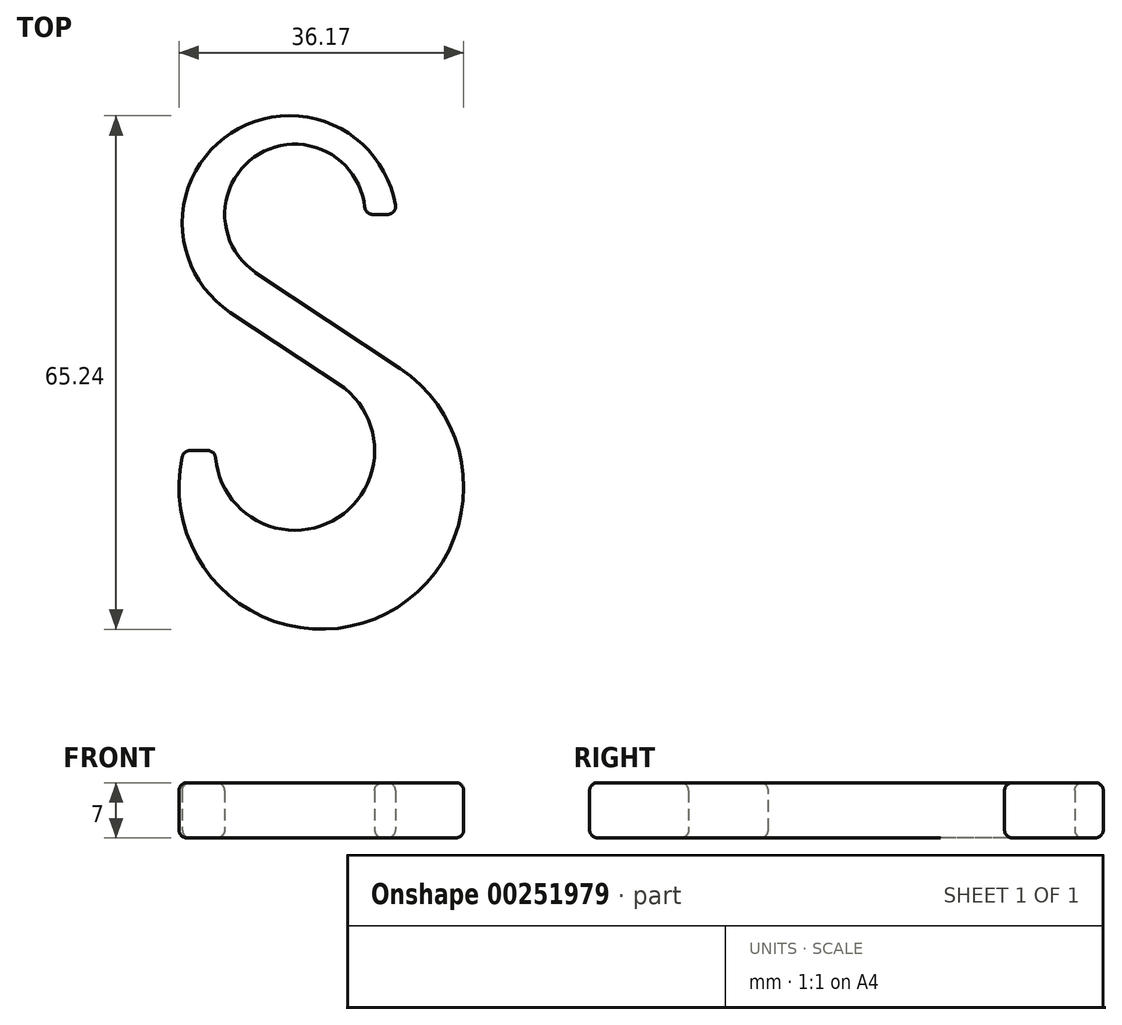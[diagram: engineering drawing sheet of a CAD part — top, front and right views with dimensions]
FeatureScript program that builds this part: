
annotation { "Feature Type Name" : "Feature", "Feature Type Description" : "" }
export const myFeature = defineFeature(function(context is Context, id is Id, definition is map)
    precondition{}
    {
        {
            var Q0;
            Q0=qCreatedBy(makeId("Top.planeOp"),FACE);
            var sketch = newSketch(context, id + "F0", { "sketchPlane" : qUnion([Q0])});
            skArc(sketch, "E0", {"start": v(8.92, 0) * mm, "mid": v(-4.16, 7.89) * mm, "end": v(-5.04, -7.35) * mm});
            skArc(sketch, "E1", {"start": v(-10.13, -30) * mm, "mid": v(4.39, -39.13) * mm, "end": v(6.33, -22.1) * mm});
            skArc(sketch, "E2.0", {"start": v(12.92, 0) * mm, "mid": v(-7.6, 10.65) * mm, "end": v(-8.2, -12.45) * mm});
            skArc(sketch, "E3.0", {"start": v(-14.13, -30) * mm, "mid": v(9.78, -51.52) * mm, "end": v(13.35, -19.55) * mm});
            skLineSegment(sketch, "E4", {"start": v(-5.04, -7.35) * mm, "end": v(13.35, -19.55) * mm});
            skLineSegment(sketch, "E5", {"start": v(-8.2, -12.45) * mm, "end": v(6.33, -22.1) * mm});
            skLineSegment(sketch, "E6", {"start": v(-14.13, -30) * mm, "end": v(-10.13, -30) * mm});
            skLineSegment(sketch, "E7", {"start": v(12.92, 0) * mm, "end": v(8.92, 0) * mm});
            skSolve(sketch);
        }
        {
            var Q0;
            Q0=makeQuery(id+"F0.imprint","IMPRINT",FACE,{"disambiguationData":[TD([[makeQuery(id+"F0.imprint","IMPRINT",EDGE,{"derivedFrom":sQuery(id+"F0.wireOp",EDGE,"E0")}),-1.0]])]});
            extrude(context, id + "F1", {"entities" : qUnion([Q0]), "depth" : 7 * mm});
        }
        {
            var Q0;
            Q0=makeQuery(id+"F1.opExtrude","SWEPT_FACE",FACE,{"disambiguationData":[OSD([sQuery(id+"F0.wireOp",EDGE,"E0")])]});
            var Q1;
            Q1=makeQuery(id+"F1.opExtrude","CAP_FACE",FACE,{"disambiguationData":[OSD([sQuery(id+"F0.wireOp",EDGE,"E0"),sQuery(id+"F0.wireOp",EDGE,"E1"),sQuery(id+"F0.wireOp",EDGE,"E2.0"),sQuery(id+"F0.wireOp",EDGE,"E3.0"),sQuery(id+"F0.wireOp",EDGE,"E4"),sQuery(id+"F0.wireOp",EDGE,"E5"),sQuery(id+"F0.wireOp",EDGE,"E6"),sQuery(id+"F0.wireOp",EDGE,"E7")])],"isStart":true});
            var Q2;
            Q2=makeQuery(id+"F1.opExtrude","CAP_FACE",FACE,{"disambiguationData":[OSD([sQuery(id+"F0.wireOp",EDGE,"E0"),sQuery(id+"F0.wireOp",EDGE,"E1"),sQuery(id+"F0.wireOp",EDGE,"E2.0"),sQuery(id+"F0.wireOp",EDGE,"E3.0"),sQuery(id+"F0.wireOp",EDGE,"E4"),sQuery(id+"F0.wireOp",EDGE,"E5"),sQuery(id+"F0.wireOp",EDGE,"E6"),sQuery(id+"F0.wireOp",EDGE,"E7")])],"isStart":false});
            var Q3;
            Q3=makeQuery(id+"F1.opExtrude","SWEPT_FACE",FACE,{"disambiguationData":[OSD([sQuery(id+"F0.wireOp",EDGE,"E1")])]});
            var Q4;
            Q4=makeQuery(id+"F1.opExtrude","SWEPT_FACE",FACE,{"disambiguationData":[OSD([sQuery(id+"F0.wireOp",EDGE,"E2.0")])]});
            var Q5;
            Q5=makeQuery(id+"F1.opExtrude","SWEPT_FACE",FACE,{"disambiguationData":[OSD([sQuery(id+"F0.wireOp",EDGE,"E3.0")])]});
            var Q6;
            Q6=makeQuery(id+"F1.opExtrude","SWEPT_FACE",FACE,{"disambiguationData":[OSD([sQuery(id+"F0.wireOp",EDGE,"E4")])]});
            var Q7;
            Q7=makeQuery(id+"F1.opExtrude","SWEPT_FACE",FACE,{"disambiguationData":[OSD([sQuery(id+"F0.wireOp",EDGE,"E5")])]});
            var Q8;
            Q8=makeQuery(id+"F1.opExtrude","SWEPT_FACE",FACE,{"disambiguationData":[OSD([sQuery(id+"F0.wireOp",EDGE,"E6")])]});
            var Q9;
            Q9=makeQuery(id+"F1.opExtrude","SWEPT_FACE",FACE,{"disambiguationData":[OSD([sQuery(id+"F0.wireOp",EDGE,"E7")])]});
            fillet(context, id + "F2", {"entities" : qUnion([Q0, Q1, Q2, Q3, Q4, Q5, Q6, Q7, Q8, Q9]), "radius" : 1 * mm, "tangentPropagation" : true, "allowEdgeOverflow" : false});
        }
    });
